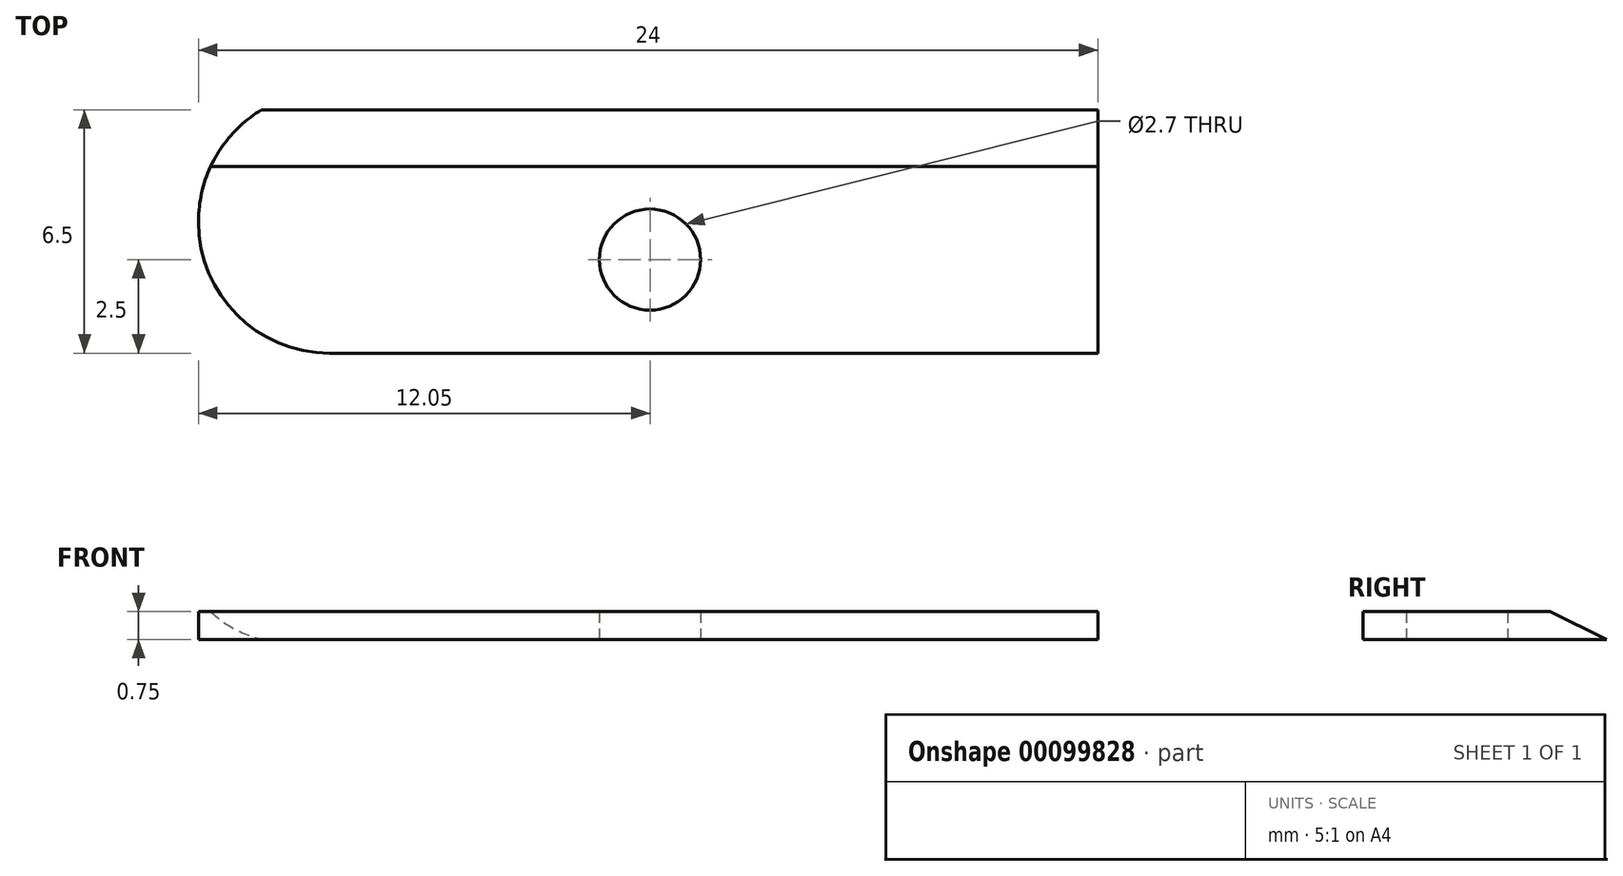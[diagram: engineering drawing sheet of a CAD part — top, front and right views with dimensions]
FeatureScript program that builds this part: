
annotation { "Feature Type Name" : "Feature", "Feature Type Description" : "" }
export const myFeature = defineFeature(function(context is Context, id is Id, definition is map)
    precondition{}
    {
        {
            var Q0;
            Q0=qCreatedBy(makeId("Top.planeOp"),FACE);
            var sketch = newSketch(context, id + "F0", { "sketchPlane" : qUnion([Q0])});
            skLineSegment(sketch, "E0", {"start": v(0, 0) * mm, "end": v(-20.5, 0) * mm});
            skCircle(sketch, "E1", {"center": v(-11.95, 2.5) * mm, "radius": 1.35 * mm});
            skLineSegment(sketch, "E2", {"start": v(-24, 3.54) * mm, "end": v(-24, 3.5) * mm});
            skArc(sketch, "E3", {"start": v(-24, 3.5) * mm, "mid": v(-22.97, 1.03) * mm, "end": v(-20.5, 0) * mm});
            skArc(sketch, "E4.trimOffspring", {"start": v(-22.32, 6.5) * mm, "mid": v(-23.56, 5.22) * mm, "end": v(-24, 3.5) * mm});
            skPoint(sketch, "E5.start.orphan", {"position": v(0, 6.5) * mm});
            skLineSegment(sketch, "E6", {"start": v(0, 6.5) * mm, "end": v(-22.32, 6.5) * mm});
            skLineSegment(sketch, "E7", {"start": v(0, 0) * mm, "end": v(0, 6.5) * mm});
            skLineSegment(sketch, "E8", {"start": v(0, 0) * mm, "end": v(0, 5) * mm});
            skLineSegment(sketch, "E9", {"start": v(0, 5) * mm, "end": v(-23.67, 5) * mm});
            skSolve(sketch);
        }
        {
            var Q0;
            Q0=makeQuery(id+"F0.imprint","IMPRINT",FACE,{"disambiguationData":[TD([[makeQuery(id+"F0.imprint","IMPRINT",EDGE,{"derivedFrom":sQuery(id+"F0.wireOp",EDGE,"E0")}),-1.0]])]});
            var Q1;
            {var subQ0=sQuery(id+"F0.wireOp",EDGE,"E6");Q1=makeQuery(id+"F0.imprint","IMPRINT",FACE,{"disambiguationData":[TD([[makeQuery(id+"F0.imprint","IMPRINT",EDGE,{"derivedFrom":subQ0}),1.0]])]});}
            extrude(context, id + "F1", {"entities" : qUnion([Q0, Q1]), "depth" : .75 * mm});
        }
        {
            var Q0;
            Q0=makeQuery(id+"F1.opExtrude","SWEPT_FACE",FACE,{"disambiguationData":[OSD([sQuery(id+"F0.wireOp",EDGE,"E7"),sQuery(id+"F0.wireOp",EDGE,"E8")])]});
            var sketch = newSketch(context, id + "F2", { "sketchPlane" : qUnion([Q0])});
            skPoint(sketch, "E10.start.orphan", {"position": v(5, 0) * mm});
            skLineSegment(sketch, "E11", {"start": v(4.99, 0.75) * mm, "end": v(6.5, 0) * mm});
            skLineSegment(sketch, "E12", {"start": v(4.99, 0.75) * mm, "end": v(6.5, 0.75) * mm});
            skLineSegment(sketch, "E13", {"start": v(6.5, 0.75) * mm, "end": v(6.5, 0) * mm});
            skSolve(sketch);
        }
        {
            var Q0;
            Q0=makeQuery(id+"F2.imprint","IMPRINT",FACE,{"disambiguationData":[TD([[makeQuery(id+"F2.imprint","IMPRINT",EDGE,{"derivedFrom":sQuery(id+"F2.wireOp",EDGE,"E11")}),1.0]])]});
            extrude(context, id + "F3", {"entities" : qUnion([Q0]), "operationType" : NewBodyOperationType.REMOVE, "endBound" : BoundingType.THROUGH_ALL, "oppositeDirection" : true, "depth" : 20 * mm});
        }
    });
